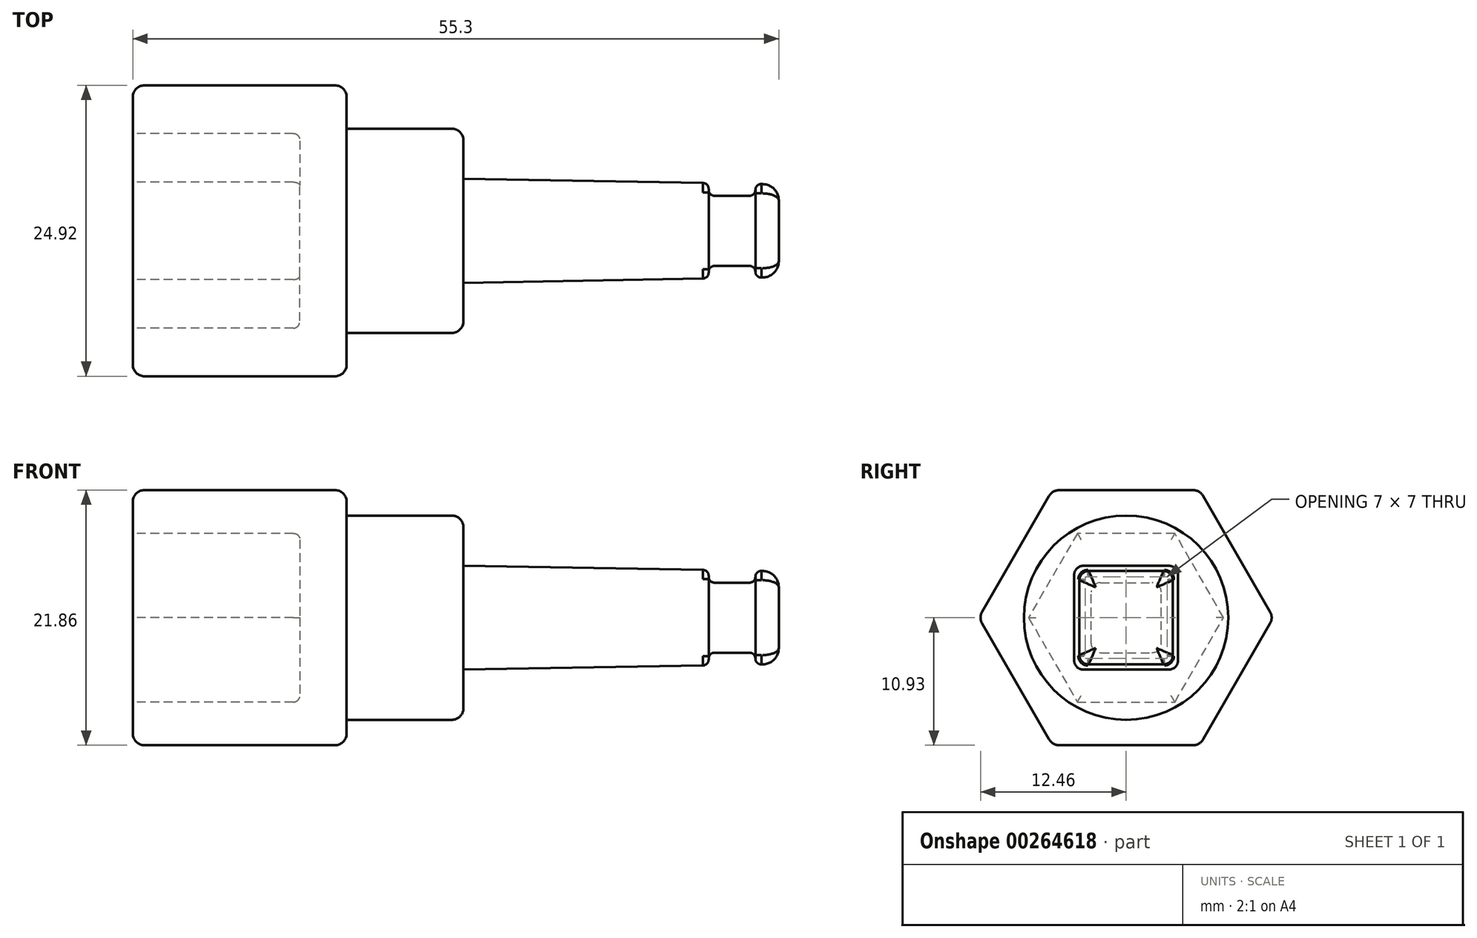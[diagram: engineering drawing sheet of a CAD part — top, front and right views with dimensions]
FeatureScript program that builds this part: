
annotation { "Feature Type Name" : "Feature", "Feature Type Description" : "" }
export const myFeature = defineFeature(function(context is Context, id is Id, definition is map)
    precondition{}
    {
        {
            var Q0;
            Q0=qCreatedBy(makeId("Right.planeOp"),FACE);
            var sketch = newSketch(context, id + "F0", { "sketchPlane" : qUnion([Q0])});
            skCircle(sketch, "E0", {"center": v(0, 0) * mm, "radius": 8.75 * mm});
            skSolve(sketch);
        }
        {
            var Q0;
            Q0 = qSketchRegion(id + "F0", true);
            extrude(context, id + "F1", {"entities" : qUnion([Q0]), "oppositeDirection" : true, "depth" : 10 * mm});
        }
        {
            var Q0;
            Q0=makeQuery(id+"F1.opExtrude","CAP_FACE",FACE,{"disambiguationData":[OSD([sQuery(id+"F0.wireOp",EDGE,"E0")])],"isStart":false});
            var sketch = newSketch(context, id + "F2", { "sketchPlane" : qUnion([Q0])});
            skCircle(sketch, "E1.cCircle", {"center": v(0, 0) * mm, "radius": 6.92 * mm, "construction": true});
            skLineSegment(sketch, "E1.0", {"start": v(4, -6.92) * mm, "end": v(-4, -6.92) * mm, "construction": true});
            skLineSegment(sketch, "E1.1", {"start": v(-4, -6.93) * mm, "end": v(-8, 0) * mm, "construction": true});
            skLineSegment(sketch, "E1.2", {"start": v(-8, 0) * mm, "end": v(-4, 6.92) * mm, "construction": true});
            skLineSegment(sketch, "E1.3", {"start": v(-4, 6.92) * mm, "end": v(4, 6.93) * mm, "construction": true});
            skLineSegment(sketch, "E1.4", {"start": v(4, 6.93) * mm, "end": v(8, 0) * mm, "construction": true});
            skLineSegment(sketch, "E1.5", {"start": v(8, 0) * mm, "end": v(4, -6.93) * mm, "construction": true});
            skPoint(sketch, "E1.0.midPoint", {"position": v(0, -6.92) * mm});
            skLineSegment(sketch, "E2.0", {"start": v(-6.3, -10.92) * mm, "end": v(-12.62, 0) * mm});
            skLineSegment(sketch, "E2.1", {"start": v(-6.3, 10.92) * mm, "end": v(6.3, 10.92) * mm});
            skLineSegment(sketch, "E2.2", {"start": v(6.3, 10.92) * mm, "end": v(12.62, 0) * mm});
            skLineSegment(sketch, "E2.3", {"start": v(-12.62, 0) * mm, "end": v(-6.3, 10.92) * mm});
            skLineSegment(sketch, "E2.4", {"start": v(12.62, 0) * mm, "end": v(6.3, -10.92) * mm});
            skLineSegment(sketch, "E2.5", {"start": v(6.3, -10.92) * mm, "end": v(-6.3, -10.92) * mm});
            skSolve(sketch);
        }
        {
            var Q0;
            Q0 = qSketchRegion(id + "F2", true);
            extrude(context, id + "F3", {"entities" : qUnion([Q0]), "operationType" : NewBodyOperationType.ADD, "depth" : 18.3 * mm});
        }
        {
            var Q0;
            Q0=makeQuery(id+"F3.opExtrude","CAP_FACE",FACE,{"disambiguationData":[OSD([sQuery(id+"F2.wireOp",EDGE,"E2.0"),sQuery(id+"F2.wireOp",EDGE,"E2.1"),sQuery(id+"F2.wireOp",EDGE,"E2.2"),sQuery(id+"F2.wireOp",EDGE,"E2.3"),sQuery(id+"F2.wireOp",EDGE,"E2.4"),sQuery(id+"F2.wireOp",EDGE,"E2.5")])],"isStart":false});
            var sketch = newSketch(context, id + "F4", { "sketchPlane" : qUnion([Q0])});
            skLineSegment(sketch, "E3.0", {"start": v(-4.17, -7.22) * mm, "end": v(-8.34, 0) * mm});
            skLineSegment(sketch, "E3.1", {"start": v(-4.17, 7.22) * mm, "end": v(4.17, 7.23) * mm});
            skLineSegment(sketch, "E3.2", {"start": v(4.17, 7.23) * mm, "end": v(8.34, 0) * mm});
            skLineSegment(sketch, "E3.3", {"start": v(-8.34, 0) * mm, "end": v(-4.17, 7.22) * mm});
            skLineSegment(sketch, "E3.4", {"start": v(8.34, 0) * mm, "end": v(4.17, -7.22) * mm});
            skLineSegment(sketch, "E3.5", {"start": v(4.17, -7.22) * mm, "end": v(-4.17, -7.22) * mm});
            skSolve(sketch);
        }
        {
            var Q0;
            Q0 = qSketchRegion(id + "F4", true);
            extrude(context, id + "F5", {"entities" : qUnion([Q0]), "operationType" : NewBodyOperationType.REMOVE, "oppositeDirection" : true, "depth" : 14.3 * mm});
        }
        {
            var Q0;
            Q0=makeQuery(id+"F1.opExtrude","CAP_FACE",FACE,{"disambiguationData":[OSD([sQuery(id+"F0.wireOp",EDGE,"E0")])],"isStart":true});
            var sketch = newSketch(context, id + "F6", { "sketchPlane" : qUnion([Q0])});
            skLineSegment(sketch, "E4.bottom", {"start": v(-4.45, -4.45) * mm, "end": v(4.45, -4.45) * mm});
            skLineSegment(sketch, "E4.top", {"start": v(-4.45, 4.45) * mm, "end": v(4.45, 4.45) * mm});
            skLineSegment(sketch, "E4.left", {"start": v(-4.45, -4.45) * mm, "end": v(-4.45, 4.45) * mm});
            skLineSegment(sketch, "E4.right", {"start": v(4.45, -4.45) * mm, "end": v(4.45, 4.45) * mm});
            skPoint(sketch, "E4.middle", {"position": v(0, 0) * mm});
            skSolve(sketch);
        }
        {
            var Q0;
            Q0 = qSketchRegion(id + "F6", true);
            extrude(context, id + "F7", {"entities" : qUnion([Q0]), "operationType" : NewBodyOperationType.ADD, "depth" : 27 * mm, "hasDraft" : true, "draftAngle" : 1 * degree, "draftPullDirection" : true});
        }
        {
            var Q0;
            Q0=makeQuery(id+"F7.opExtrude","SWEPT_EDGE",EDGE,{"disambiguationData":[OSD([sQuery(id+"F6.wireOp",EDGE,"E4.top"),sQuery(id+"F6.wireOp",EDGE,"E4.left")])]});
            var Q1;
            Q1=makeQuery(id+"F7.opExtrude","SWEPT_EDGE",EDGE,{"disambiguationData":[OSD([sQuery(id+"F6.wireOp",EDGE,"E4.top"),sQuery(id+"F6.wireOp",EDGE,"E4.right")])]});
            var Q2;
            Q2=makeQuery(id+"F7.opExtrude","SWEPT_EDGE",EDGE,{"disambiguationData":[OSD([sQuery(id+"F6.wireOp",EDGE,"E4.bottom"),sQuery(id+"F6.wireOp",EDGE,"E4.right")])]});
            var Q3;
            Q3=makeQuery(id+"F7.opExtrude","SWEPT_EDGE",EDGE,{"disambiguationData":[OSD([sQuery(id+"F6.wireOp",EDGE,"E4.bottom"),sQuery(id+"F6.wireOp",EDGE,"E4.left")])]});
            fillet(context, id + "F8", {"entities" : qUnion([Q0, Q1, Q2, Q3]), "radius" : .8 * mm, "tangentPropagation" : true, "allowEdgeOverflow" : false});
        }
        {
            var Q0;
            Q0=makeQuery(id+"F7.opExtrude","CAP_FACE",FACE,{"disambiguationData":[OSD([sQuery(id+"F6.wireOp",EDGE,"E4.bottom"),sQuery(id+"F6.wireOp",EDGE,"E4.top"),sQuery(id+"F6.wireOp",EDGE,"E4.left"),sQuery(id+"F6.wireOp",EDGE,"E4.right")])],"isStart":false});
            var sketch = newSketch(context, id + "F9", { "sketchPlane" : qUnion([Q0])});
            skLineSegment(sketch, "E5.bottom", {"start": v(-3, -3) * mm, "end": v(3, -3) * mm});
            skLineSegment(sketch, "E5.top", {"start": v(-3, 3) * mm, "end": v(3, 3) * mm});
            skLineSegment(sketch, "E5.left", {"start": v(-3, -3) * mm, "end": v(-3, 3) * mm});
            skLineSegment(sketch, "E5.right", {"start": v(3, -3) * mm, "end": v(3, 3) * mm});
            skPoint(sketch, "E5.middle", {"position": v(0, 0) * mm});
            skLineSegment(sketch, "E6.bottom", {"start": v(-5, -5) * mm, "end": v(5, -5) * mm});
            skLineSegment(sketch, "E6.top", {"start": v(-5, 5) * mm, "end": v(5, 5) * mm});
            skLineSegment(sketch, "E6.left", {"start": v(-5, -5) * mm, "end": v(-5, 5) * mm});
            skLineSegment(sketch, "E6.right", {"start": v(5, -5) * mm, "end": v(5, 5) * mm});
            skSolve(sketch);
        }
        {
            var Q0;
            Q0=makeQuery(id+"F7.opExtrude","CAP_FACE",FACE,{"disambiguationData":[OSD([sQuery(id+"F6.wireOp",EDGE,"E4.bottom"),sQuery(id+"F6.wireOp",EDGE,"E4.top"),sQuery(id+"F6.wireOp",EDGE,"E4.left"),sQuery(id+"F6.wireOp",EDGE,"E4.right")])],"isStart":false});
            cPlane(context, id + "F10", {"entities" : qUnion([Q0]), "cplaneType" : CPlaneType.OFFSET, "offset" : 2 * mm, "oppositeDirection" : true, "width" : 150 * mm, "height" : 150 * mm});
        }
        {
            var Q0;
            Q0=qCreatedBy(id+"F10.planeOp",FACE);
            var sketch = newSketch(context, id + "F11", { "sketchPlane" : qUnion([Q0])});
            skLineSegment(sketch, "E7.0", {"start": v(-3, -3) * mm, "end": v(3, -3) * mm});
            skLineSegment(sketch, "E7.1", {"start": v(-3, 3) * mm, "end": v(3, 3) * mm});
            skLineSegment(sketch, "E7.2", {"start": v(-3, -3) * mm, "end": v(-3, 3) * mm});
            skLineSegment(sketch, "E7.3", {"start": v(3, -3) * mm, "end": v(3, 3) * mm});
            skPoint(sketch, "E7.4", {"position": v(0, 0) * mm});
            skLineSegment(sketch, "E7.5", {"start": v(-5, -5) * mm, "end": v(5, -5) * mm});
            skLineSegment(sketch, "E7.6", {"start": v(-5, 5) * mm, "end": v(5, 5) * mm});
            skLineSegment(sketch, "E7.7", {"start": v(-5, -5) * mm, "end": v(-5, 5) * mm});
            skLineSegment(sketch, "E7.8", {"start": v(5, -5) * mm, "end": v(5, 5) * mm});
            skPoint(sketch, "E7.9", {"position": v(0, 0) * mm});
            skSolve(sketch);
        }
        {
            var Q0;
            Q0 = qSketchRegion(id + "F11", true);
            extrude(context, id + "F12", {"entities" : qUnion([Q0]), "operationType" : NewBodyOperationType.REMOVE, "oppositeDirection" : true, "depth" : 4 * mm});
        }
        {
            var Q0;
            Q0=makeQuery(id+"F12.boolean.opBoolean","COPY",EDGE,{"derivedFrom":makeQuery(id+"F12.opExtrude","SWEPT_EDGE",EDGE,{"disambiguationData":[OSD([sQuery(id+"F11.wireOp",EDGE,"E7.1"),sQuery(id+"F11.wireOp",EDGE,"E7.2")])]})});
            var Q1;
            Q1=makeQuery(id+"F12.boolean.opBoolean","COPY",EDGE,{"derivedFrom":makeQuery(id+"F12.opExtrude","SWEPT_EDGE",EDGE,{"disambiguationData":[OSD([sQuery(id+"F11.wireOp",EDGE,"E7.1"),sQuery(id+"F11.wireOp",EDGE,"E7.3")])]})});
            var Q2;
            Q2=makeQuery(id+"F12.boolean.opBoolean","COPY",EDGE,{"derivedFrom":makeQuery(id+"F12.opExtrude","SWEPT_EDGE",EDGE,{"disambiguationData":[OSD([sQuery(id+"F11.wireOp",EDGE,"E7.0"),sQuery(id+"F11.wireOp",EDGE,"E7.3")])]})});
            var Q3;
            Q3=makeQuery(id+"F12.boolean.opBoolean","COPY",EDGE,{"derivedFrom":makeQuery(id+"F12.opExtrude","SWEPT_EDGE",EDGE,{"disambiguationData":[OSD([sQuery(id+"F11.wireOp",EDGE,"E7.0"),sQuery(id+"F11.wireOp",EDGE,"E7.2")])]})});
            fillet(context, id + "F13", {"entities" : qUnion([Q0, Q1, Q2, Q3]), "radius" : .8 * mm, "tangentPropagation" : true, "allowEdgeOverflow" : false});
        }
        {
            var Q0;
            Q0=makeQuery(id+"F12.boolean.opBoolean","INTERSECT",EDGE,{"derivedFrom":[makeQuery(id+"F7.opExtrude","SWEPT_FACE",FACE,{"disambiguationData":[OSD([sQuery(id+"F6.wireOp",EDGE,"E4.top")])]}),makeQuery(id+"F12.opExtrude","CAP_FACE",FACE,{"disambiguationData":[OSD([sQuery(id+"F11.wireOp",EDGE,"E7.0"),sQuery(id+"F11.wireOp",EDGE,"E7.1"),sQuery(id+"F11.wireOp",EDGE,"E7.2"),sQuery(id+"F11.wireOp",EDGE,"E7.3"),sQuery(id+"F11.wireOp",EDGE,"E7.5"),sQuery(id+"F11.wireOp",EDGE,"E7.6"),sQuery(id+"F11.wireOp",EDGE,"E7.7"),sQuery(id+"F11.wireOp",EDGE,"E7.8")])],"isStart":true})]});
            var Q1;
            Q1=makeQuery(id+"F12.boolean.opBoolean","INTERSECT",EDGE,{"derivedFrom":[makeQuery(id+"F7.opExtrude","SWEPT_FACE",FACE,{"disambiguationData":[OSD([sQuery(id+"F6.wireOp",EDGE,"E4.left")])]}),makeQuery(id+"F12.opExtrude","CAP_FACE",FACE,{"disambiguationData":[OSD([sQuery(id+"F11.wireOp",EDGE,"E7.0"),sQuery(id+"F11.wireOp",EDGE,"E7.1"),sQuery(id+"F11.wireOp",EDGE,"E7.2"),sQuery(id+"F11.wireOp",EDGE,"E7.3"),sQuery(id+"F11.wireOp",EDGE,"E7.5"),sQuery(id+"F11.wireOp",EDGE,"E7.6"),sQuery(id+"F11.wireOp",EDGE,"E7.7"),sQuery(id+"F11.wireOp",EDGE,"E7.8")])],"isStart":true})]});
            fillet(context, id + "F14", {"entities" : qUnion([Q0, Q1]), "radius" : .5 * mm, "tangentPropagation" : true, "allowEdgeOverflow" : false});
        }
        {
            var Q0;
            Q0=makeQuery(id+"F12.boolean.opBoolean","COPY",EDGE,{"derivedFrom":makeQuery(id+"F12.opExtrude","CAP_EDGE",EDGE,{"disambiguationData":[OSD([sQuery(id+"F11.wireOp",EDGE,"E7.1")])],"isStart":true})});
            var Q1;
            Q1=makeQuery(id+"F12.boolean.opBoolean","COPY",EDGE,{"derivedFrom":makeQuery(id+"F12.opExtrude","CAP_EDGE",EDGE,{"disambiguationData":[OSD([sQuery(id+"F11.wireOp",EDGE,"E7.1")])],"isStart":false})});
            var Q2;
            Q2=makeQuery(id+"F12.boolean.opBoolean","INTERSECT",EDGE,{"derivedFrom":[makeQuery(id+"F7.opExtrude","SWEPT_FACE",FACE,{"disambiguationData":[OSD([sQuery(id+"F6.wireOp",EDGE,"E4.top")])]}),makeQuery(id+"F12.opExtrude","CAP_FACE",FACE,{"disambiguationData":[OSD([sQuery(id+"F11.wireOp",EDGE,"E7.0"),sQuery(id+"F11.wireOp",EDGE,"E7.1"),sQuery(id+"F11.wireOp",EDGE,"E7.2"),sQuery(id+"F11.wireOp",EDGE,"E7.3"),sQuery(id+"F11.wireOp",EDGE,"E7.5"),sQuery(id+"F11.wireOp",EDGE,"E7.6"),sQuery(id+"F11.wireOp",EDGE,"E7.7"),sQuery(id+"F11.wireOp",EDGE,"E7.8")])],"isStart":false})]});
            fillet(context, id + "F15", {"entities" : qUnion([Q0, Q1, Q2]), "radius" : .5 * mm, "tangentPropagation" : true, "allowEdgeOverflow" : false});
        }
        {
            var Q0;
            Q0=makeQuery(id+"F7.opExtrude","CAP_FACE",FACE,{"disambiguationData":[OSD([sQuery(id+"F6.wireOp",EDGE,"E4.bottom"),sQuery(id+"F6.wireOp",EDGE,"E4.top"),sQuery(id+"F6.wireOp",EDGE,"E4.left"),sQuery(id+"F6.wireOp",EDGE,"E4.right")])],"isStart":false});
            fillet(context, id + "F16", {"entities" : qUnion([Q0]), "radius" : 1.4 * mm, "tangentPropagation" : true, "allowEdgeOverflow" : false});
        }
        {
            var Q0;
            Q0=makeQuery(id+"F7.opExtrude","CAP_EDGE",EDGE,{"disambiguationData":[OSD([sQuery(id+"F6.wireOp",EDGE,"E4.left")])],"isStart":true});
            var Q1;
            Q1=makeQuery(id+"F1.opExtrude","CAP_EDGE",EDGE,{"disambiguationData":[OSD([sQuery(id+"F0.wireOp",EDGE,"E0")])],"isStart":false});
            var Q2;
            Q2=makeQuery(id+"F1.opExtrude","CAP_EDGE",EDGE,{"disambiguationData":[OSD([sQuery(id+"F0.wireOp",EDGE,"E0")])],"isStart":true});
            fillet(context, id + "F17", {"entities" : qUnion([Q0, Q1, Q2]), "radius" : 1 * mm, "tangentPropagation" : true, "allowEdgeOverflow" : false});
        }
        {
            var Q0;
            Q0=makeQuery(id+"F3.opExtrude","SWEPT_EDGE",EDGE,{"disambiguationData":[OSD([sQuery(id+"F2.wireOp",EDGE,"E2.1"),sQuery(id+"F2.wireOp",EDGE,"E2.2")])]});
            var Q1;
            Q1=makeQuery(id+"F3.opExtrude","SWEPT_EDGE",EDGE,{"disambiguationData":[OSD([sQuery(id+"F2.wireOp",EDGE,"E2.2"),sQuery(id+"F2.wireOp",EDGE,"E2.4")])]});
            var Q2;
            Q2=makeQuery(id+"F3.opExtrude","SWEPT_EDGE",EDGE,{"disambiguationData":[OSD([sQuery(id+"F2.wireOp",EDGE,"E2.1"),sQuery(id+"F2.wireOp",EDGE,"E2.3")])]});
            var Q3;
            Q3=makeQuery(id+"F3.opExtrude","SWEPT_EDGE",EDGE,{"disambiguationData":[OSD([sQuery(id+"F2.wireOp",EDGE,"E2.4"),sQuery(id+"F2.wireOp",EDGE,"E2.5")])]});
            var Q4;
            Q4=makeQuery(id+"F3.opExtrude","SWEPT_EDGE",EDGE,{"disambiguationData":[OSD([sQuery(id+"F2.wireOp",EDGE,"E2.0"),sQuery(id+"F2.wireOp",EDGE,"E2.3")])]});
            var Q5;
            Q5=makeQuery(id+"F3.opExtrude","SWEPT_EDGE",EDGE,{"disambiguationData":[OSD([sQuery(id+"F2.wireOp",EDGE,"E2.0"),sQuery(id+"F2.wireOp",EDGE,"E2.5")])]});
            var Q6;
            Q6=makeQuery(id+"F3.opExtrude","CAP_EDGE",EDGE,{"disambiguationData":[OSD([sQuery(id+"F2.wireOp",EDGE,"E2.3")])],"isStart":true});
            var Q7;
            Q7=makeQuery(id+"F3.opExtrude","CAP_EDGE",EDGE,{"disambiguationData":[OSD([sQuery(id+"F2.wireOp",EDGE,"E2.1")])],"isStart":true});
            var Q8;
            Q8=makeQuery(id+"F3.opExtrude","CAP_EDGE",EDGE,{"disambiguationData":[OSD([sQuery(id+"F2.wireOp",EDGE,"E2.2")])],"isStart":true});
            var Q9;
            Q9=makeQuery(id+"F3.opExtrude","CAP_EDGE",EDGE,{"disambiguationData":[OSD([sQuery(id+"F2.wireOp",EDGE,"E2.0")])],"isStart":true});
            var Q10;
            Q10=makeQuery(id+"F3.opExtrude","CAP_EDGE",EDGE,{"disambiguationData":[OSD([sQuery(id+"F2.wireOp",EDGE,"E2.5")])],"isStart":true});
            var Q11;
            Q11=makeQuery(id+"F3.opExtrude","CAP_EDGE",EDGE,{"disambiguationData":[OSD([sQuery(id+"F2.wireOp",EDGE,"E2.4")])],"isStart":true});
            var Q12;
            Q12=makeQuery(id+"F3.opExtrude","CAP_EDGE",EDGE,{"disambiguationData":[OSD([sQuery(id+"F2.wireOp",EDGE,"E2.4")])],"isStart":false});
            var Q13;
            Q13=makeQuery(id+"F3.opExtrude","CAP_EDGE",EDGE,{"disambiguationData":[OSD([sQuery(id+"F2.wireOp",EDGE,"E2.2")])],"isStart":false});
            var Q14;
            Q14=makeQuery(id+"F3.opExtrude","CAP_EDGE",EDGE,{"disambiguationData":[OSD([sQuery(id+"F2.wireOp",EDGE,"E2.1")])],"isStart":false});
            var Q15;
            Q15=makeQuery(id+"F3.opExtrude","CAP_EDGE",EDGE,{"disambiguationData":[OSD([sQuery(id+"F2.wireOp",EDGE,"E2.3")])],"isStart":false});
            var Q16;
            Q16=makeQuery(id+"F3.opExtrude","CAP_EDGE",EDGE,{"disambiguationData":[OSD([sQuery(id+"F2.wireOp",EDGE,"E2.0")])],"isStart":false});
            var Q17;
            Q17=makeQuery(id+"F3.opExtrude","CAP_EDGE",EDGE,{"disambiguationData":[OSD([sQuery(id+"F2.wireOp",EDGE,"E2.5")])],"isStart":false});
            fillet(context, id + "F18", {"entities" : qUnion([Q0, Q1, Q2, Q3, Q4, Q5, Q6, Q7, Q8, Q9, Q10, Q11, Q12, Q13, Q14, Q15, Q16, Q17]), "radius" : 1 * mm, "tangentPropagation" : true, "allowEdgeOverflow" : false});
        }
        {
            var Q0;
            Q0=makeQuery(id+"F5.boolean.opBoolean","COPY",EDGE,{"derivedFrom":makeQuery(id+"F5.opExtrude","CAP_EDGE",EDGE,{"disambiguationData":[OSD([sQuery(id+"F4.wireOp",EDGE,"E3.3")])],"isStart":true})});
            var Q1;
            Q1=makeQuery(id+"F5.boolean.opBoolean","COPY",EDGE,{"derivedFrom":makeQuery(id+"F5.opExtrude","CAP_EDGE",EDGE,{"disambiguationData":[OSD([sQuery(id+"F4.wireOp",EDGE,"E3.0")])],"isStart":true})});
            var Q2;
            Q2=makeQuery(id+"F5.boolean.opBoolean","COPY",EDGE,{"derivedFrom":makeQuery(id+"F5.opExtrude","CAP_EDGE",EDGE,{"disambiguationData":[OSD([sQuery(id+"F4.wireOp",EDGE,"E3.1")])],"isStart":true})});
            var Q3;
            Q3=makeQuery(id+"F5.boolean.opBoolean","COPY",EDGE,{"derivedFrom":makeQuery(id+"F5.opExtrude","CAP_EDGE",EDGE,{"disambiguationData":[OSD([sQuery(id+"F4.wireOp",EDGE,"E3.2")])],"isStart":true})});
            var Q4;
            Q4=makeQuery(id+"F5.boolean.opBoolean","COPY",EDGE,{"derivedFrom":makeQuery(id+"F5.opExtrude","CAP_EDGE",EDGE,{"disambiguationData":[OSD([sQuery(id+"F4.wireOp",EDGE,"E3.4")])],"isStart":true})});
            var Q5;
            Q5=makeQuery(id+"F5.boolean.opBoolean","COPY",EDGE,{"derivedFrom":makeQuery(id+"F5.opExtrude","CAP_EDGE",EDGE,{"disambiguationData":[OSD([sQuery(id+"F4.wireOp",EDGE,"E3.5")])],"isStart":true})});
            var Q6;
            Q6=makeQuery(id+"F5.boolean.opBoolean","COPY",FACE,{"derivedFrom":makeQuery(id+"F5.opExtrude","CAP_FACE",FACE,{"disambiguationData":[OSD([sQuery(id+"F4.wireOp",EDGE,"E3.0"),sQuery(id+"F4.wireOp",EDGE,"E3.1"),sQuery(id+"F4.wireOp",EDGE,"E3.2"),sQuery(id+"F4.wireOp",EDGE,"E3.3"),sQuery(id+"F4.wireOp",EDGE,"E3.4"),sQuery(id+"F4.wireOp",EDGE,"E3.5")])],"isStart":false})});
            fillet(context, id + "F19", {"entities" : qUnion([Q0, Q1, Q2, Q3, Q4, Q5, Q6]), "radius" : .55 * mm, "tangentPropagation" : true, "allowEdgeOverflow" : false});
        }
    });
